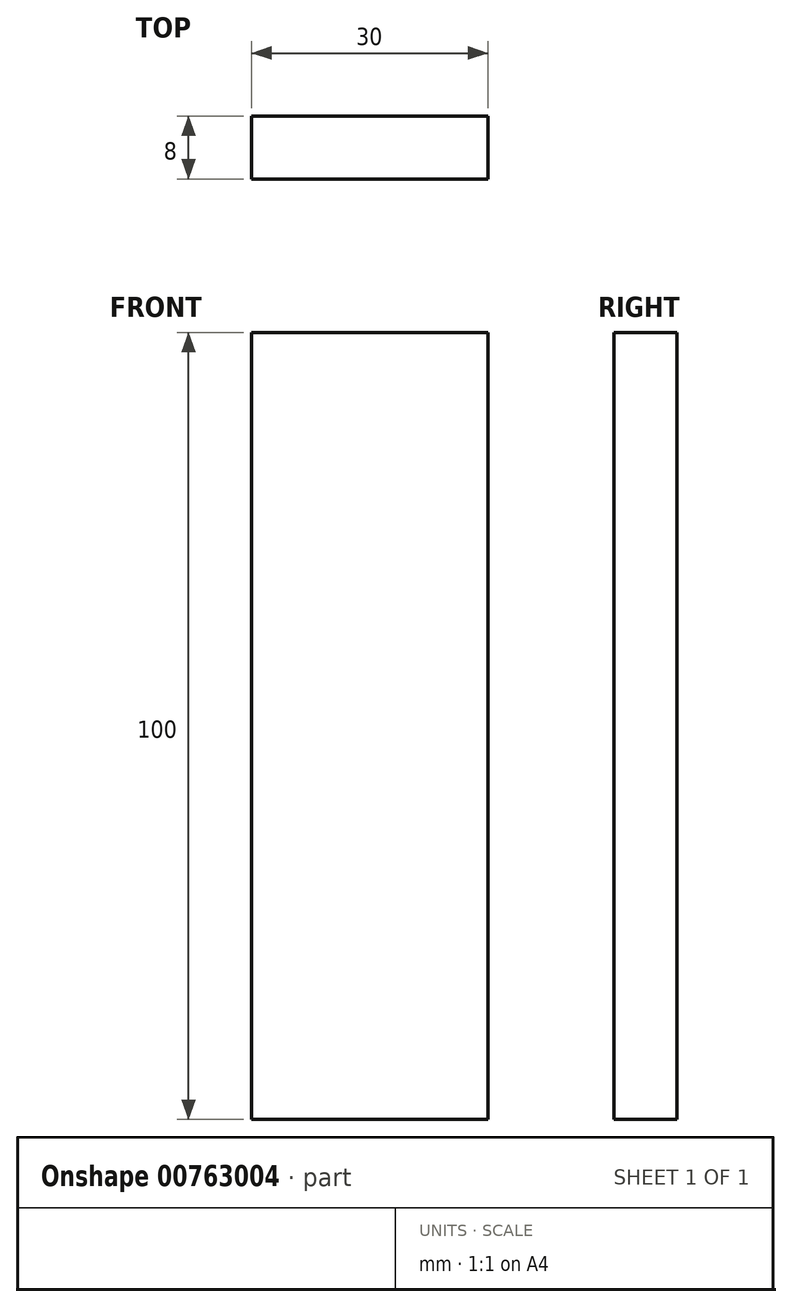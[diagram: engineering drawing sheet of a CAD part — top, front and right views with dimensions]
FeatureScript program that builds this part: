
annotation { "Feature Type Name" : "Feature", "Feature Type Description" : "" }
export const myFeature = defineFeature(function(context is Context, id is Id, definition is map)
    precondition{}
    {
        {
            var Q0;
            Q0=qCreatedBy(makeId("Front.planeOp"),FACE);
            var sketch = newSketch(context, id + "F0", { "sketchPlane" : qUnion([Q0])});
            skLineSegment(sketch, "E0.bottom", {"start": v(-15, -50) * mm, "end": v(15, -50) * mm});
            skLineSegment(sketch, "E0.top", {"start": v(-15, 50) * mm, "end": v(15, 50) * mm});
            skLineSegment(sketch, "E0.left", {"start": v(-15, -50) * mm, "end": v(-15, 50) * mm});
            skLineSegment(sketch, "E0.right", {"start": v(15, -50) * mm, "end": v(15, 50) * mm});
            skLineSegment(sketch, "E1", {"start": v(0, 50) * mm, "end": v(0, -50) * mm, "construction": true});
            skSolve(sketch);
        }
        {
            var Q0;
            Q0=makeQuery(id+"F0.imprint","IMPRINT",FACE,{"disambiguationData":[TD([[makeQuery(id+"F0.imprint","IMPRINT",EDGE,{"derivedFrom":sQuery(id+"F0.wireOp",EDGE,"E0.bottom")}),1.0]])]});
            extrude(context, id + "F1", {"entities" : qUnion([Q0]), "endBound" : BoundingType.SYMMETRIC, "depth" : 8 * mm, "offsetDistance" : 25 * mm});
        }
    });
